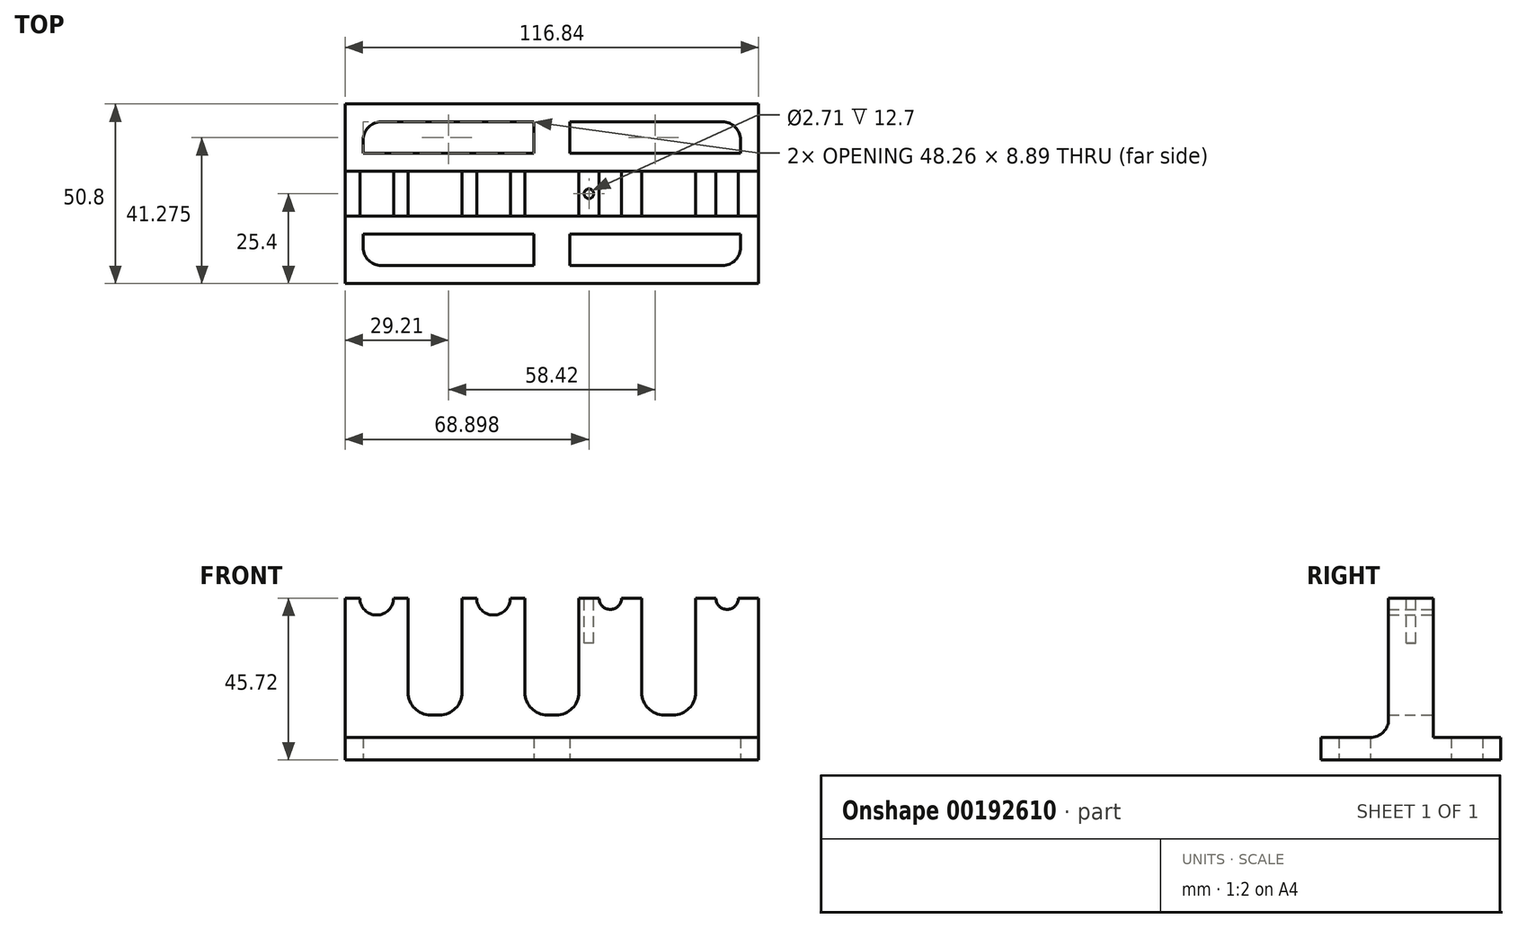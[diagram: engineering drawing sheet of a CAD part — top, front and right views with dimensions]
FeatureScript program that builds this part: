
annotation { "Feature Type Name" : "Feature", "Feature Type Description" : "" }
export const myFeature = defineFeature(function(context is Context, id is Id, definition is map)
    precondition{}
    {
        {
            var Q0;
            Q0=qCreatedBy(makeId("Front.planeOp"),FACE);
            var sketch = newSketch(context, id + "F0", { "sketchPlane" : qUnion([Q0])});
            skArc(sketch, "E0", {"start": v(-4.76, 0) * mm, "mid": v(0, -4.76) * mm, "end": v(4.76, 0) * mm});
            skArc(sketch, "E1", {"start": v(28.26, 0) * mm, "mid": v(33.02, -4.76) * mm, "end": v(37.78, 0) * mm});
            skArc(sketch, "E2", {"start": v(62.87, 0) * mm, "mid": v(66.04, -3.17) * mm, "end": v(69.22, 0) * mm});
            skArc(sketch, "E3", {"start": v(95.89, 0) * mm, "mid": v(99.06, -3.17) * mm, "end": v(102.24, 0) * mm});
            skLineSegment(sketch, "E4.bottom", {"start": v(-8.9, 0) * mm, "end": v(-4.76, 0) * mm});
            skLineSegment(sketch, "E4.top", {"start": v(-8.89, -45.72) * mm, "end": v(107.95, -45.72) * mm});
            skLineSegment(sketch, "E4.left", {"start": v(-8.9, 0) * mm, "end": v(-8.89, -45.72) * mm});
            skLineSegment(sketch, "E4.right", {"start": v(107.95, 0) * mm, "end": v(107.95, -45.72) * mm});
            skLineSegment(sketch, "E5.top", {"start": v(15.24, -33.02) * mm, "end": v(17.78, -33.02) * mm});
            skLineSegment(sketch, "E5.left", {"start": v(8.9, 0) * mm, "end": v(8.9, -26.67) * mm});
            skLineSegment(sketch, "E5.right", {"start": v(24.13, 0) * mm, "end": v(24.13, -26.67) * mm});
            skLineSegment(sketch, "E6.top", {"start": v(48.26, -33.02) * mm, "end": v(50.8, -33.02) * mm});
            skLineSegment(sketch, "E6.left", {"start": v(41.91, 0) * mm, "end": v(41.91, -26.67) * mm});
            skLineSegment(sketch, "E6.right", {"start": v(57.15, 0) * mm, "end": v(57.15, -26.67) * mm});
            skLineSegment(sketch, "E7.top", {"start": v(81.28, -33.02) * mm, "end": v(83.82, -33.02) * mm});
            skLineSegment(sketch, "E7.left", {"start": v(74.93, 0) * mm, "end": v(74.93, -26.67) * mm});
            skLineSegment(sketch, "E7.right", {"start": v(90.17, 0) * mm, "end": v(90.17, -26.67) * mm});
            skLineSegment(sketch, "E8.trimOffspring", {"start": v(24.13, 0) * mm, "end": v(28.26, 0) * mm});
            skLineSegment(sketch, "E9.trimOffspring", {"start": v(57.15, 0) * mm, "end": v(62.87, 0) * mm});
            skLineSegment(sketch, "E10.trimOffspring", {"start": v(90.17, 0) * mm, "end": v(95.89, 0) * mm});
            skLineSegment(sketch, "E11.trimOffspring", {"start": v(4.76, 0) * mm, "end": v(8.9, 0) * mm});
            skLineSegment(sketch, "E12.trimOffspring", {"start": v(37.78, 0) * mm, "end": v(41.91, 0) * mm});
            skLineSegment(sketch, "E13.trimOffspring", {"start": v(69.22, 0) * mm, "end": v(74.93, 0) * mm});
            skLineSegment(sketch, "E14.trimOffspring", {"start": v(102.24, 0) * mm, "end": v(107.95, 0) * mm});
            skPoint(sketch, "E15.visualSharp", {"position": v(8.9, -33.02) * mm});
            skArc(sketch, "E15.filletArc", {"start": v(8.9, -26.67) * mm, "mid": v(10.75, -31.16) * mm, "end": v(15.24, -33.02) * mm});
            skPoint(sketch, "E16.visualSharp", {"position": v(24.13, -33.02) * mm});
            skArc(sketch, "E16.filletArc", {"start": v(17.78, -33.02) * mm, "mid": v(22.27, -31.16) * mm, "end": v(24.13, -26.67) * mm});
            skPoint(sketch, "E17.visualSharp", {"position": v(41.91, -33.02) * mm});
            skArc(sketch, "E17.filletArc", {"start": v(41.91, -26.67) * mm, "mid": v(43.77, -31.16) * mm, "end": v(48.26, -33.02) * mm});
            skPoint(sketch, "E18.visualSharp", {"position": v(57.15, -33.02) * mm});
            skArc(sketch, "E18.filletArc", {"start": v(50.8, -33.02) * mm, "mid": v(55.3, -31.16) * mm, "end": v(57.15, -26.67) * mm});
            skPoint(sketch, "E19.visualSharp", {"position": v(74.93, -33.02) * mm});
            skArc(sketch, "E19.filletArc", {"start": v(74.93, -26.67) * mm, "mid": v(76.79, -31.16) * mm, "end": v(81.28, -33.02) * mm});
            skPoint(sketch, "E20.visualSharp", {"position": v(90.17, -33.02) * mm});
            skArc(sketch, "E20.filletArc", {"start": v(83.82, -33.02) * mm, "mid": v(88.31, -31.16) * mm, "end": v(90.17, -26.67) * mm});
            skLineSegment(sketch, "E21.top", {"start": v(-8.9, -39.37) * mm, "end": v(107.95, -39.37) * mm});
            skLineSegment(sketch, "E21.left", {"start": v(-8.89, -45.72) * mm, "end": v(-8.89, -39.37) * mm});
            skLineSegment(sketch, "E21.right", {"start": v(107.95, -45.72) * mm, "end": v(107.95, -39.37) * mm});
            skSolve(sketch);
        }
        {
            var Q0;
            Q0=makeQuery(id+"F0.imprint","IMPRINT",FACE,{"disambiguationData":[TD([[makeQuery(id+"F0.imprint","IMPRINT",EDGE,{"derivedFrom":sQuery(id+"F0.wireOp",EDGE,"E0")}),-1.0]])]});
            extrude(context, id + "F1", {"entities" : qUnion([Q0]), "endBound" : BoundingType.SYMMETRIC, "depth" : 12.7 * mm});
        }
        {
            var Q0;
            Q0=makeQuery(id+"F0.imprint","IMPRINT",FACE,{"disambiguationData":[TD([[makeQuery(id+"F0.imprint","IMPRINT",EDGE,{"derivedFrom":sQuery(id+"F0.wireOp",EDGE,"E4.top")}),1.0]])]});
            extrude(context, id + "F2", {"entities" : qUnion([Q0]), "operationType" : NewBodyOperationType.ADD, "endBound" : BoundingType.SYMMETRIC, "depth" : 50.8 * mm});
        }
        {
            var Q0;
            Q0=makeQuery(id+"F1.opExtrude","CAP_EDGE",EDGE,{"disambiguationData":[OSD([sQuery(id+"F0.wireOp",EDGE,"E21.top")])],"isStart":false});
            var Q1;
            Q1=makeQuery(id+"F1.opExtrude","CAP_EDGE",EDGE,{"disambiguationData":[OSD([sQuery(id+"F0.wireOp",EDGE,"E21.top")])],"isStart":true});
            var Q2;
            Q2=makeQuery(id+"F2.opExtrude","CAP_EDGE",EDGE,{"disambiguationData":[OSD([sQuery(id+"F0.wireOp",EDGE,"E21.right")])],"isStart":false});
            var Q3;
            Q3=makeQuery(id+"F2.opExtrude","CAP_EDGE",EDGE,{"disambiguationData":[OSD([sQuery(id+"F0.wireOp",EDGE,"E21.left")])],"isStart":false});
            var Q4;
            Q4=makeQuery(id+"F2.opExtrude","CAP_EDGE",EDGE,{"disambiguationData":[OSD([sQuery(id+"F0.wireOp",EDGE,"E21.right")])],"isStart":true});
            var Q5;
            Q5=makeQuery(id+"F2.opExtrude","CAP_EDGE",EDGE,{"disambiguationData":[OSD([sQuery(id+"F0.wireOp",EDGE,"E21.left")])],"isStart":true});
            fillet(context, id + "F3", {"entities" : qUnion([Q0, Q1, Q2, Q3, Q4, Q5]), "radius" : 5.08 * mm, "tangentPropagation" : true, "allowEdgeOverflow" : false});
        }
        {
            var Q0;
            Q0=makeQuery(id+"F2.opExtrude","SWEPT_FACE",FACE,{"disambiguationData":[OSD([sQuery(id+"F0.wireOp",EDGE,"E4.top")])]});
            var sketch = newSketch(context, id + "F4", { "sketchPlane" : qUnion([Q0])});
            skLineSegment(sketch, "E22.bottom", {"start": v(-3.8, 20.32) * mm, "end": v(44.45, 20.32) * mm});
            skLineSegment(sketch, "E22.top", {"start": v(-3.81, 11.43) * mm, "end": v(44.45, 11.43) * mm});
            skLineSegment(sketch, "E22.left", {"start": v(-3.8, 20.32) * mm, "end": v(-3.8, 11.43) * mm});
            skLineSegment(sketch, "E22.right", {"start": v(44.45, 20.32) * mm, "end": v(44.45, 11.43) * mm});
            skLineSegment(sketch, "E23", {"start": v(49.53, 25.4) * mm, "end": v(49.53, -25.4) * mm, "construction": true});
            skLineSegment(sketch, "E24.MirrorCS", {"start": v(54.61, 20.32) * mm, "end": v(54.61, 11.43) * mm});
            skLineSegment(sketch, "E25.MirrorCS", {"start": v(102.87, 20.32) * mm, "end": v(102.87, 11.43) * mm});
            skLineSegment(sketch, "E26.MirrorCS", {"start": v(102.87, 11.43) * mm, "end": v(54.61, 11.43) * mm});
            skLineSegment(sketch, "E27.MirrorCS", {"start": v(102.87, 20.32) * mm, "end": v(54.61, 20.32) * mm});
            skLineSegment(sketch, "E28.MirrorCS", {"start": v(102.87, -20.32) * mm, "end": v(54.61, -20.32) * mm});
            skLineSegment(sketch, "E29.MirrorCS", {"start": v(102.87, -11.43) * mm, "end": v(54.61, -11.43) * mm});
            skLineSegment(sketch, "E30.MirrorCS", {"start": v(102.87, -20.32) * mm, "end": v(102.87, -11.43) * mm});
            skLineSegment(sketch, "E31.MirrorCS", {"start": v(-3.8, -20.32) * mm, "end": v(44.45, -20.32) * mm});
            skLineSegment(sketch, "E32.MirrorCS", {"start": v(-3.81, -11.43) * mm, "end": v(44.45, -11.43) * mm});
            skLineSegment(sketch, "E33.MirrorCS", {"start": v(-3.8, -20.32) * mm, "end": v(-3.8, -11.43) * mm});
            skLineSegment(sketch, "E34.MirrorCS", {"start": v(44.45, -20.32) * mm, "end": v(44.45, -11.43) * mm});
            skLineSegment(sketch, "E35.MirrorCS", {"start": v(54.61, -20.32) * mm, "end": v(54.61, -11.43) * mm});
            skSolve(sketch);
        }
        {
            var Q0;
            Q0 = qSketchRegion(id + "F4", true);
            extrude(context, id + "F5", {"entities" : qUnion([Q0]), "operationType" : NewBodyOperationType.REMOVE, "oppositeDirection" : true, "depth" : 25.4 * mm});
        }
        {
            var Q0;
            Q0=makeQuery(id+"F5.boolean.opBoolean","COPY",EDGE,{"derivedFrom":makeQuery(id+"F5.opExtrude","SWEPT_EDGE",EDGE,{"disambiguationData":[OSD([sQuery(id+"F4.wireOp",EDGE,"E31.MirrorCS"),sQuery(id+"F4.wireOp",EDGE,"E33.MirrorCS")])]})});
            var Q1;
            Q1=makeQuery(id+"F5.boolean.opBoolean","COPY",EDGE,{"derivedFrom":makeQuery(id+"F5.opExtrude","SWEPT_EDGE",EDGE,{"disambiguationData":[OSD([sQuery(id+"F4.wireOp",EDGE,"E28.MirrorCS"),sQuery(id+"F4.wireOp",EDGE,"E30.MirrorCS")])]})});
            var Q2;
            Q2=makeQuery(id+"F5.boolean.opBoolean","COPY",EDGE,{"derivedFrom":makeQuery(id+"F5.opExtrude","SWEPT_EDGE",EDGE,{"disambiguationData":[OSD([sQuery(id+"F4.wireOp",EDGE,"E22.bottom"),sQuery(id+"F4.wireOp",EDGE,"E22.left")])]})});
            var Q3;
            Q3=makeQuery(id+"F5.boolean.opBoolean","COPY",EDGE,{"derivedFrom":makeQuery(id+"F5.opExtrude","SWEPT_EDGE",EDGE,{"disambiguationData":[OSD([sQuery(id+"F4.wireOp",EDGE,"E25.MirrorCS"),sQuery(id+"F4.wireOp",EDGE,"E27.MirrorCS")])]})});
            fillet(context, id + "F6", {"entities" : qUnion([Q0, Q1, Q2, Q3]), "radius" : 5.08 * mm, "tangentPropagation" : true, "allowEdgeOverflow" : false});
        }
        {
            var Q0;
            Q0=makeQuery(id+"F1.opExtrude","SWEPT_FACE",FACE,{"disambiguationData":[OSD([sQuery(id+"F0.wireOp",EDGE,"E9.trimOffspring")])]});
            var sketch = newSketch(context, id + "F7", { "sketchPlane" : qUnion([Q0])});
            skCircle(sketch, "E36", {"center": v(60, 0) * mm, "radius": 1.35 * mm});
            skSolve(sketch);
        }
        {
            var Q0;
            Q0 = qSketchRegion(id + "F7", true);
            extrude(context, id + "F8", {"entities" : qUnion([Q0]), "operationType" : NewBodyOperationType.REMOVE, "oppositeDirection" : true, "depth" : 12.7 * mm});
        }
    });
